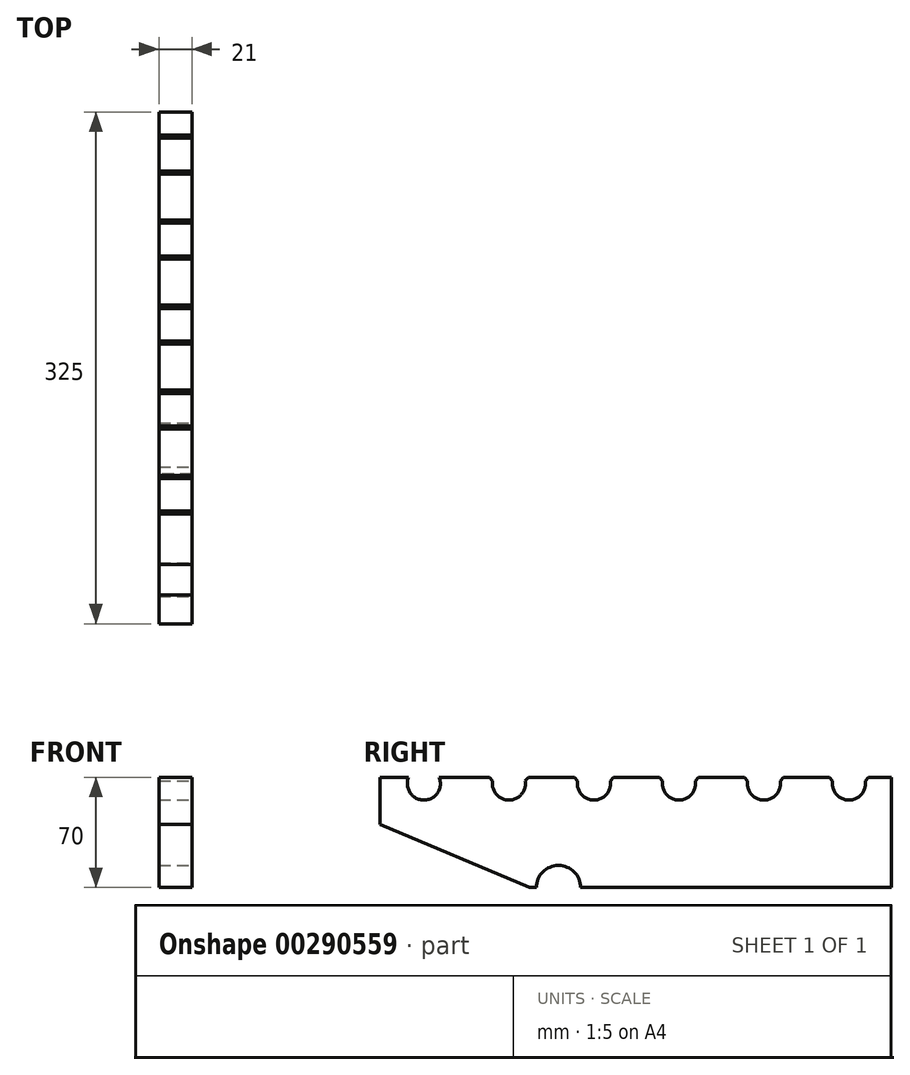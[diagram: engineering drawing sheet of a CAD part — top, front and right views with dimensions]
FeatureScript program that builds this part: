
annotation { "Feature Type Name" : "Feature", "Feature Type Description" : "" }
export const myFeature = defineFeature(function(context is Context, id is Id, definition is map)
    precondition{}
    {
        {
            var Q0;
            Q0=qCreatedBy(makeId("Right.planeOp"),FACE);
            var sketch = newSketch(context, id + "F0", { "sketchPlane" : qUnion([Q0])});
            skLineSegment(sketch, "E0", {"start": v(-135, -3.54) * mm, "end": v(-135, 26.46) * mm});
            skLineSegment(sketch, "E1", {"start": v(-135, 26.46) * mm, "end": v(190, 26.46) * mm});
            skLineSegment(sketch, "E2", {"start": v(190, 26.46) * mm, "end": v(190, -43.54) * mm});
            skLineSegment(sketch, "E3", {"start": v(-135, -3.54) * mm, "end": v(-40, -43.54) * mm});
            skLineSegment(sketch, "E4", {"start": v(-40, -43.54) * mm, "end": v(190, -43.54) * mm});
            skSolve(sketch);
        }
        {
            var Q0;
            Q0=qSketchRegion(id+"F0",true);
            extrude(context, id + "F1", {"entities" : qUnion([Q0]), "depth" : 21 * mm});
        }
        {
            var Q0;
            Q0=makeQuery(id+"F1.opExtrude","CAP_FACE",FACE,{"disambiguationData":[OSD([sQuery(id+"F0.wireOp",EDGE,"5eda4d90-05a8-43b5-b0d5-cd3ae59d76b5"),sQuery(id+"F0.wireOp",EDGE,"E0"),sQuery(id+"F0.wireOp",EDGE,"E1"),sQuery(id+"F0.wireOp",EDGE,"E2")])],"isStart":false});
            var sketch = newSketch(context, id + "F2", { "sketchPlane" : qUnion([Q0])});
            skLineSegment(sketch, "E5", {"start": v(155.2, 22.46) * mm, "end": v(-167.63, 22.46) * mm, "construction": true});
            skCircle(sketch, "E6", {"center": v(163, 22.46) * mm, "radius": 10.5 * mm});
            skCircle(sketch, "E7.1.0.0", {"center": v(109, 22.46) * mm, "radius": 10.5 * mm});
            skLineSegment(sketch, "E7.1.0.1", {"start": v(101.2, 22.46) * mm, "end": v(-221.63, 22.46) * mm, "construction": true});
            skCircle(sketch, "E7.2.0.0", {"center": v(55, 22.46) * mm, "radius": 10.5 * mm});
            skLineSegment(sketch, "E7.2.0.1", {"start": v(47.2, 22.46) * mm, "end": v(-275.63, 22.46) * mm, "construction": true});
            skCircle(sketch, "E7.3.0.0", {"center": v(1, 22.46) * mm, "radius": 10.5 * mm});
            skLineSegment(sketch, "E7.3.0.1", {"start": v(-6.8, 22.46) * mm, "end": v(-329.63, 22.46) * mm, "construction": true});
            skCircle(sketch, "E7.4.0.0", {"center": v(-53, 22.46) * mm, "radius": 10.5 * mm});
            skLineSegment(sketch, "E7.4.0.1", {"start": v(-60.8, 22.46) * mm, "end": v(-383.63, 22.46) * mm, "construction": true});
            skLineSegment(sketch, "E7.direction1", {"start": v(163, 22.46) * mm, "end": v(109, 22.46) * mm, "construction": true});
            skCircle(sketch, "E8.0.5.0", {"center": v(-107, 22.46) * mm, "radius": 10.5 * mm});
            skLineSegment(sketch, "E8.2.5.0", {"start": v(-114.8, 22.46) * mm, "end": v(-437.63, 22.46) * mm, "construction": true});
            skSolve(sketch);
        }
        {
            var Q0;
            Q0=qSketchRegion(id+"F2",true);
            extrude(context, id + "F3", {"entities" : qUnion([Q0]), "operationType" : NewBodyOperationType.REMOVE, "oppositeDirection" : true, "depth" : 25 * mm});
        }
        {
            var Q0;
            Q0=makeQuery(id+"F3.boolean.opBoolean","INTERSECT",EDGE,{"disambiguationData":[OD(1.0)],"derivedFrom":[makeQuery(id+"F1.opExtrude","SWEPT_FACE",FACE,{"disambiguationData":[OSD([sQuery(id+"F0.wireOp",EDGE,"E1")])]}),makeQuery(id+"F3.opExtrude","SWEPT_FACE",FACE,{"disambiguationData":[OSD([sQuery(id+"F2.wireOp",EDGE,"E7.4.0.0")])]})]});
            var Q1;
            Q1=makeQuery(id+"F3.boolean.opBoolean","INTERSECT",EDGE,{"disambiguationData":[OD(0.0)],"derivedFrom":[makeQuery(id+"F1.opExtrude","SWEPT_FACE",FACE,{"disambiguationData":[OSD([sQuery(id+"F0.wireOp",EDGE,"E1")])]}),makeQuery(id+"F3.opExtrude","SWEPT_FACE",FACE,{"disambiguationData":[OSD([sQuery(id+"F2.wireOp",EDGE,"E7.4.0.0")])]})]});
            var Q2;
            Q2=makeQuery(id+"F3.boolean.opBoolean","INTERSECT",EDGE,{"disambiguationData":[OD(1.0)],"derivedFrom":[makeQuery(id+"F1.opExtrude","SWEPT_FACE",FACE,{"disambiguationData":[OSD([sQuery(id+"F0.wireOp",EDGE,"E1")])]}),makeQuery(id+"F3.opExtrude","SWEPT_FACE",FACE,{"disambiguationData":[OSD([sQuery(id+"F2.wireOp",EDGE,"E7.3.0.0")])]})]});
            var Q3;
            Q3=makeQuery(id+"F3.boolean.opBoolean","INTERSECT",EDGE,{"disambiguationData":[OD(0.0)],"derivedFrom":[makeQuery(id+"F1.opExtrude","SWEPT_FACE",FACE,{"disambiguationData":[OSD([sQuery(id+"F0.wireOp",EDGE,"E1")])]}),makeQuery(id+"F3.opExtrude","SWEPT_FACE",FACE,{"disambiguationData":[OSD([sQuery(id+"F2.wireOp",EDGE,"E7.3.0.0")])]})]});
            var Q4;
            Q4=makeQuery(id+"F3.boolean.opBoolean","INTERSECT",EDGE,{"disambiguationData":[OD(1.0)],"derivedFrom":[makeQuery(id+"F1.opExtrude","SWEPT_FACE",FACE,{"disambiguationData":[OSD([sQuery(id+"F0.wireOp",EDGE,"E1")])]}),makeQuery(id+"F3.opExtrude","SWEPT_FACE",FACE,{"disambiguationData":[OSD([sQuery(id+"F2.wireOp",EDGE,"E7.2.0.0")])]})]});
            var Q5;
            Q5=makeQuery(id+"F3.boolean.opBoolean","INTERSECT",EDGE,{"disambiguationData":[OD(0.0)],"derivedFrom":[makeQuery(id+"F1.opExtrude","SWEPT_FACE",FACE,{"disambiguationData":[OSD([sQuery(id+"F0.wireOp",EDGE,"E1")])]}),makeQuery(id+"F3.opExtrude","SWEPT_FACE",FACE,{"disambiguationData":[OSD([sQuery(id+"F2.wireOp",EDGE,"E7.2.0.0")])]})]});
            var Q6;
            Q6=makeQuery(id+"F3.boolean.opBoolean","INTERSECT",EDGE,{"disambiguationData":[OD(1.0)],"derivedFrom":[makeQuery(id+"F1.opExtrude","SWEPT_FACE",FACE,{"disambiguationData":[OSD([sQuery(id+"F0.wireOp",EDGE,"E1")])]}),makeQuery(id+"F3.opExtrude","SWEPT_FACE",FACE,{"disambiguationData":[OSD([sQuery(id+"F2.wireOp",EDGE,"E7.1.0.0")])]})]});
            var Q7;
            Q7=makeQuery(id+"F3.boolean.opBoolean","INTERSECT",EDGE,{"disambiguationData":[OD(0.0)],"derivedFrom":[makeQuery(id+"F1.opExtrude","SWEPT_FACE",FACE,{"disambiguationData":[OSD([sQuery(id+"F0.wireOp",EDGE,"E1")])]}),makeQuery(id+"F3.opExtrude","SWEPT_FACE",FACE,{"disambiguationData":[OSD([sQuery(id+"F2.wireOp",EDGE,"E7.1.0.0")])]})]});
            var Q8;
            Q8=makeQuery(id+"F3.boolean.opBoolean","INTERSECT",EDGE,{"disambiguationData":[OD(1.0)],"derivedFrom":[makeQuery(id+"F1.opExtrude","SWEPT_FACE",FACE,{"disambiguationData":[OSD([sQuery(id+"F0.wireOp",EDGE,"E1")])]}),makeQuery(id+"F3.opExtrude","SWEPT_FACE",FACE,{"disambiguationData":[OSD([sQuery(id+"F2.wireOp",EDGE,"E6")])]})]});
            var Q9;
            Q9=makeQuery(id+"F3.boolean.opBoolean","INTERSECT",EDGE,{"disambiguationData":[OD(0.0)],"derivedFrom":[makeQuery(id+"F1.opExtrude","SWEPT_FACE",FACE,{"disambiguationData":[OSD([sQuery(id+"F0.wireOp",EDGE,"E1")])]}),makeQuery(id+"F3.opExtrude","SWEPT_FACE",FACE,{"disambiguationData":[OSD([sQuery(id+"F2.wireOp",EDGE,"E6")])]})]});
            chamfer(context, id + "F4", {"entities" : qUnion([Q0, Q1, Q2, Q3, Q4, Q5, Q6, Q7, Q8, Q9]), "width" : 2 * mm, "tangentPropagation" : true});
        }
        {
            var Q0;
            Q0=makeQuery(id+"F1.opExtrude","CAP_FACE",FACE,{"disambiguationData":[OSD([sQuery(id+"F0.wireOp",EDGE,"E0"),sQuery(id+"F0.wireOp",EDGE,"E1"),sQuery(id+"F0.wireOp",EDGE,"E2"),sQuery(id+"F0.wireOp",EDGE,"E3"),sQuery(id+"F0.wireOp",EDGE,"E4")])],"isStart":false});
            var sketch = newSketch(context, id + "F5", { "sketchPlane" : qUnion([Q0])});
            skCircle(sketch, "E9", {"center": v(-21.5, -43.54) * mm, "radius": 14 * mm});
            skSolve(sketch);
        }
        {
            var Q0;
            Q0 = qSketchRegion(id + "F5", true);
            extrude(context, id + "F6", {"entities" : qUnion([Q0]), "operationType" : NewBodyOperationType.REMOVE, "oppositeDirection" : true, "depth" : 25 * mm});
        }
    });
